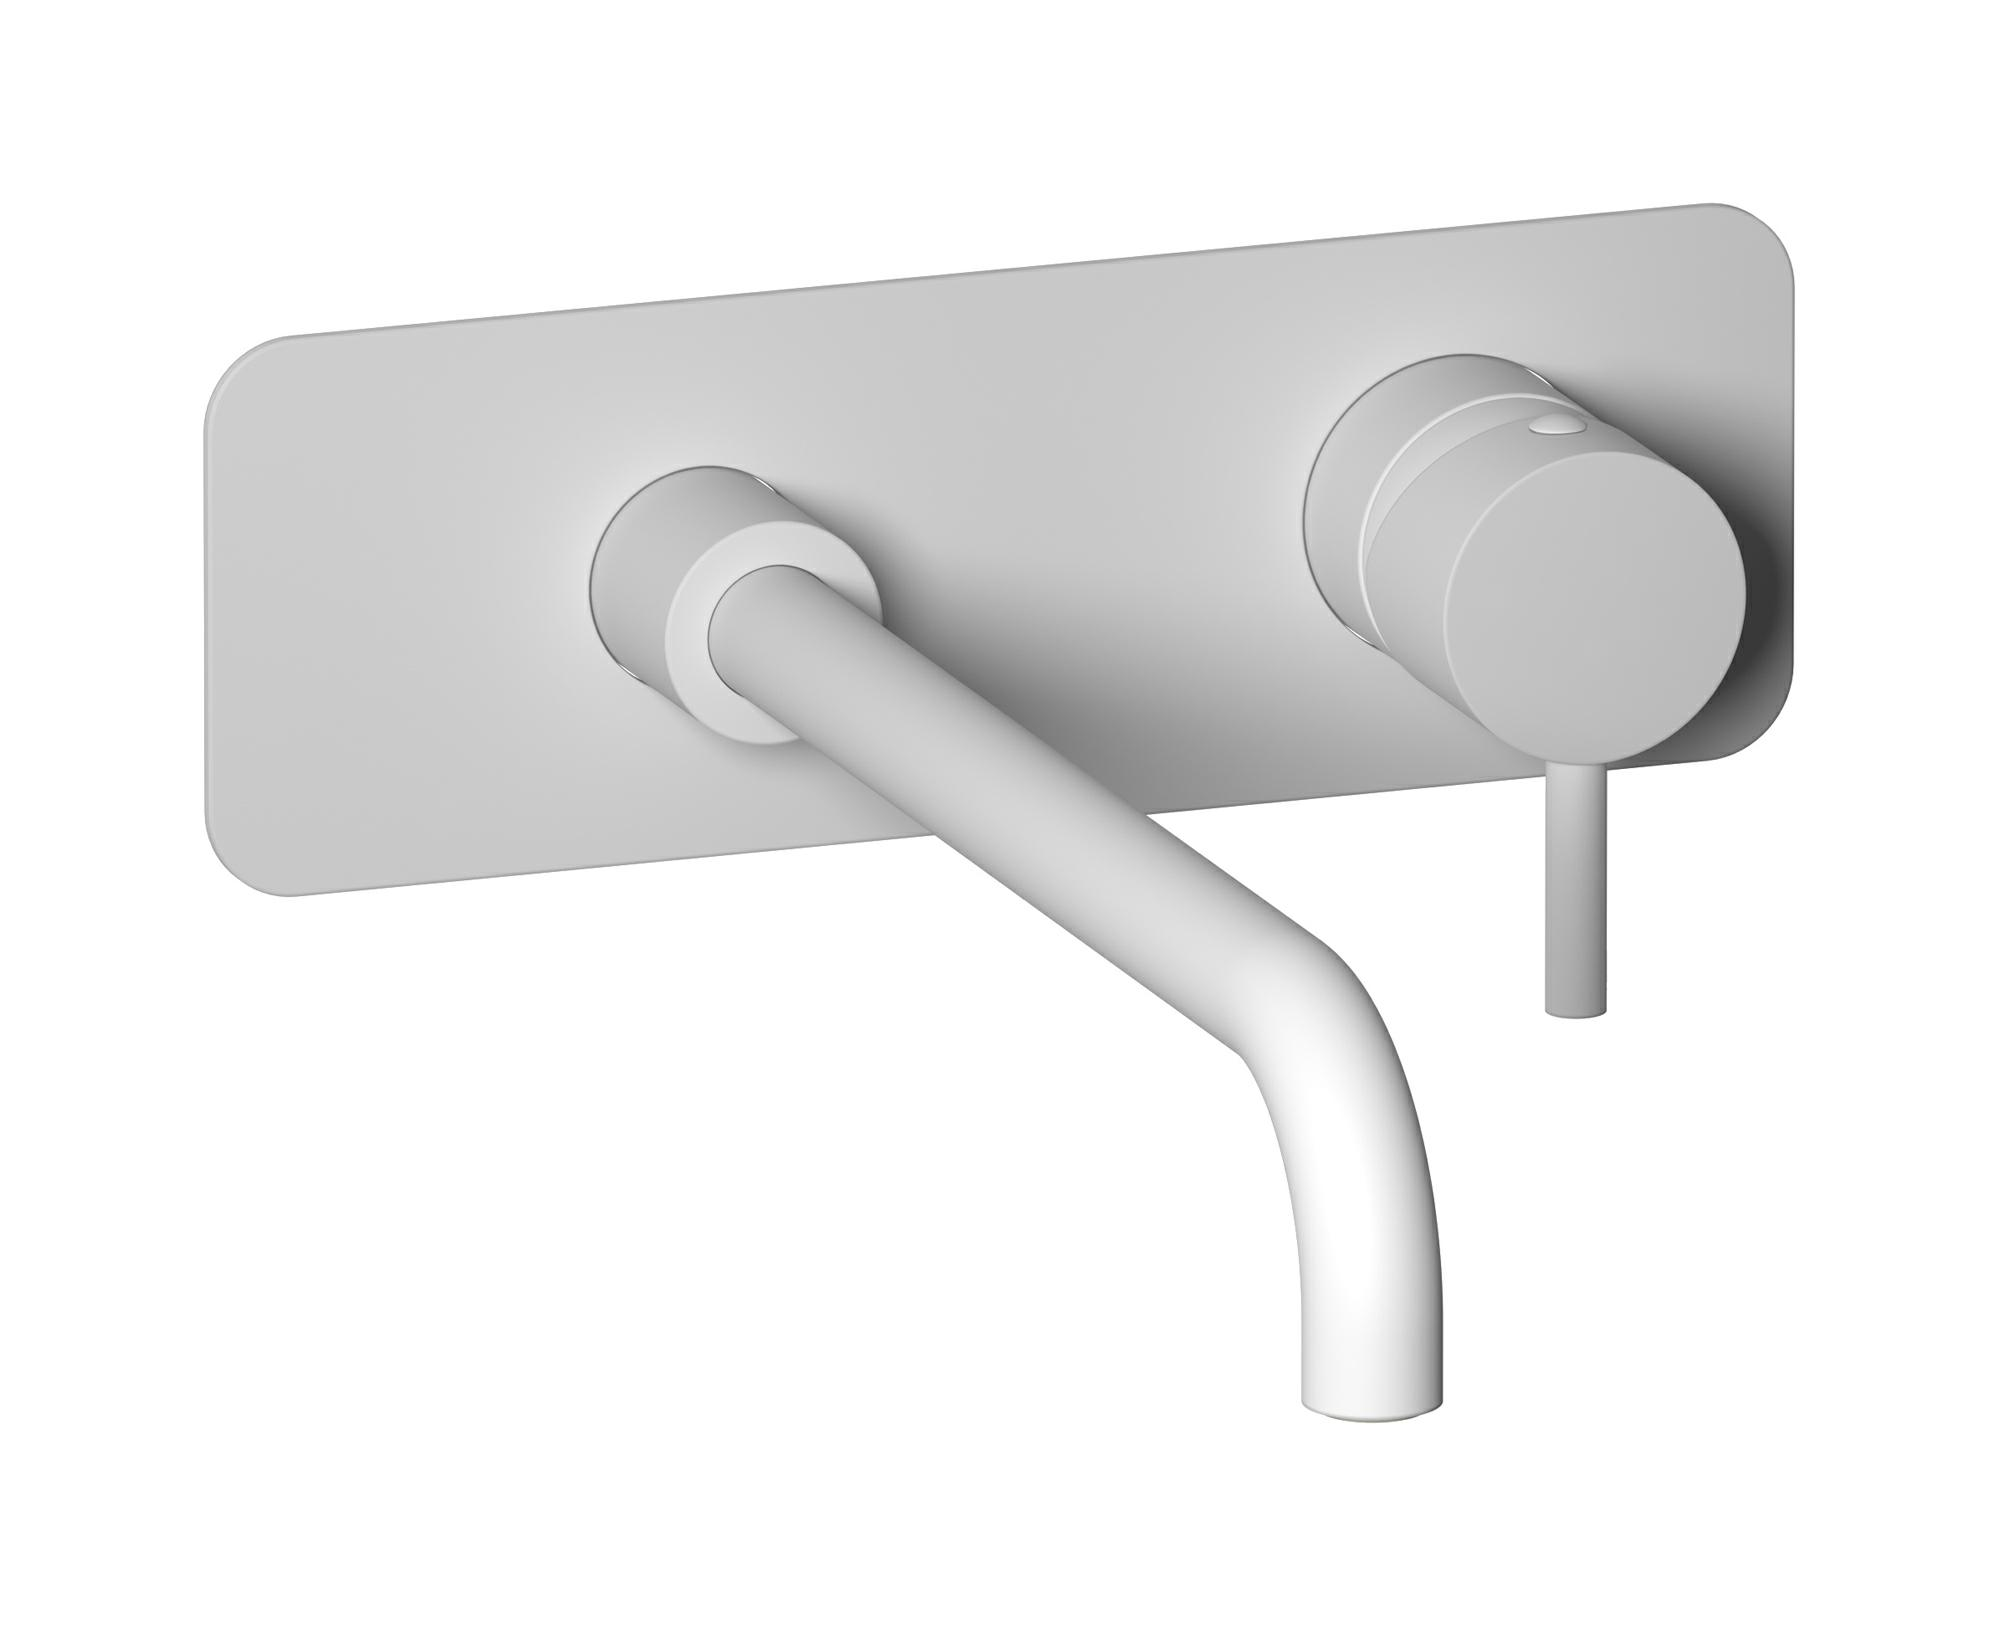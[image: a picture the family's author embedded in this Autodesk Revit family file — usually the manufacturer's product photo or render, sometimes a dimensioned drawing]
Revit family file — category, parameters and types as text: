
# Revit family: MT207
name_source: partatom
category: Apparecchi idraulici
units: mm (PartAtom-declared; Revit-internal decimal feet)

## family parameters
Basato su piano di lavoro = No
Condiviso = No
Mantieni orientamento annotazione = No
Numero OmniClass = 23.45.55.17
Punto di calcolo locali = No
Quota connettore circolare = Usa diametro
Sempre verticale = Sì
Taglio con vuoti quando caricato = No
Tipo di parte = Normale
Titolo OmniClass = Mixing Faucets

## types (12) — shared parameters
Cold water inlet = 10 mm  [stored 0.0328084 ft]
Commenti sul tipo = Washbasin mixer
Connessione CW = No
Connessione HW = No
Connessione di scarico = No
Connessione di ventilazione = No
Descrizione = Wall mounted washbasin mixer with long spout complete with drain
Hot water inlet = 10 mm  [stored 0.0328084 ft]
Produttore = IB Rubinetterie S.p.A.
URL = https://www.weareib.it
zero-valued in all types: Prospetto di default

## per-type parameters (varying)
| type | Finishes surface | Immagine tipo | Modello |
| Chrome | IB_Chrome | MT207CC.jpg | MT207CC |
| Brushed nickel | IB_Brushed nickel | MT207SS.jpg | MT207SS |
| Matt white | IB_matt white | MT207BO.jpg | MT207BO |
| Matt black | IB_matt black | MT207NP.jpg | MT207NP |
| Black chrome | IB_Black chrome | MT207CF.jpg | MT207CF |
| Brushed black chrome | IB_Brushed black chrome | MT207CS.jpg | MT207CS |
| Pale gold | IB_Pale gold | MT207II.jpg | MT207II |
| Brushed pale gold | IB_brushed pale gold | MT207IS.jpg | MT207IS |
| Rose gold | IB_Rose gold | MT207RS.jpg | MT207RS |
| Brushed rose gold | IB_Brushed rose gold | MT207SR.jpg | MT207SR |
| Gold | IB_gold | MT207OO.jpg | MT207OO |
| Brushed gold | IB_brushed gold | MT207OS.jpg | MT207OS |

note: [stored X ft] marks values corroborated as IEEE doubles in the binary element streams (Revit-internal decimal feet)
